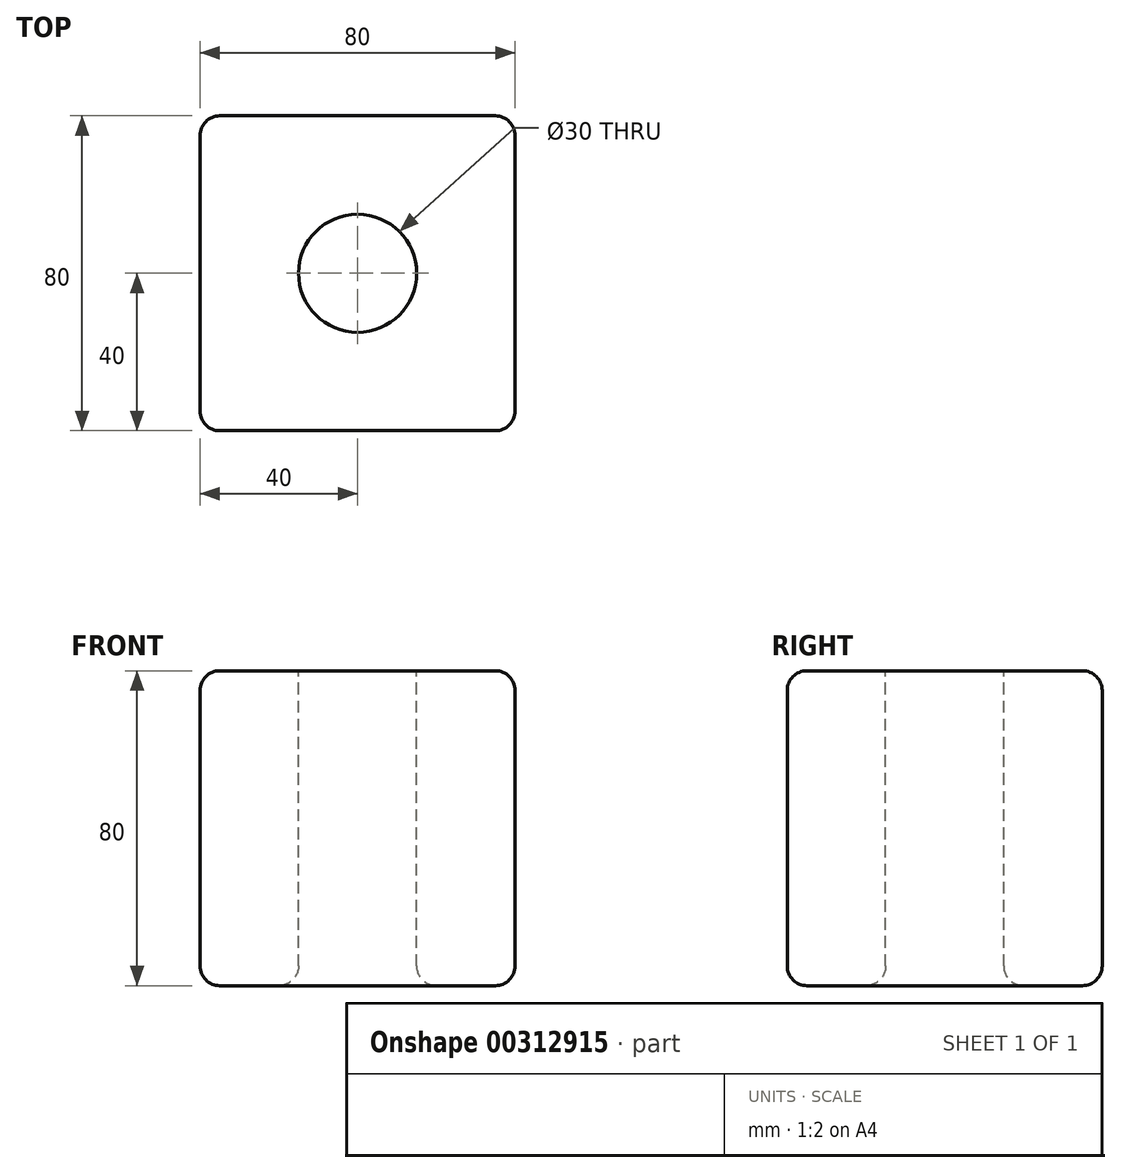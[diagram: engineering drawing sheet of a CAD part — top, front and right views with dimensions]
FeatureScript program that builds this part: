
annotation { "Feature Type Name" : "Feature", "Feature Type Description" : "" }
export const myFeature = defineFeature(function(context is Context, id is Id, definition is map)
    precondition{}
    {
        {
            var Q0;
            Q0=qCreatedBy(makeId("Top.planeOp"),FACE);
            var sketch = newSketch(context, id + "F0", { "sketchPlane" : qUnion([Q0])});
            skLineSegment(sketch, "E0.bottom", {"start": v(40, -40) * mm, "end": v(-40, -40) * mm});
            skLineSegment(sketch, "E0.top", {"start": v(40, 40) * mm, "end": v(-40, 40) * mm});
            skLineSegment(sketch, "E0.left", {"start": v(40, -40) * mm, "end": v(40, 40) * mm});
            skLineSegment(sketch, "E0.right", {"start": v(-40, -40) * mm, "end": v(-40, 40) * mm});
            skPoint(sketch, "E0.middle", {"position": v(0, 0) * mm});
            skSolve(sketch);
        }
        {
            var Q0;
            Q0=makeQuery(id+"F0.imprint","IMPRINT",FACE,{"disambiguationData":[TD([[makeQuery(id+"F0.imprint","IMPRINT",EDGE,{"derivedFrom":sQuery(id+"F0.wireOp",EDGE,"E0.bottom")}),-1.0]])]});
            extrude(context, id + "F1", {"entities" : qUnion([Q0]), "endBound" : BoundingType.SYMMETRIC, "depth" : 80 * mm});
        }
        {
            var Q0;
            Q0=makeQuery(id+"F1.opExtrude","CAP_EDGE",EDGE,{"disambiguationData":[OSD([sQuery(id+"F0.wireOp",EDGE,"E0.bottom")])],"isStart":false});
            var Q1;
            Q1=makeQuery(id+"F1.opExtrude","CAP_EDGE",EDGE,{"disambiguationData":[OSD([sQuery(id+"F0.wireOp",EDGE,"E0.bottom")])],"isStart":true});
            var Q2;
            Q2=makeQuery(id+"F1.opExtrude","CAP_EDGE",EDGE,{"disambiguationData":[OSD([sQuery(id+"F0.wireOp",EDGE,"E0.top")])],"isStart":false});
            var Q3;
            Q3=makeQuery(id+"F1.opExtrude","CAP_EDGE",EDGE,{"disambiguationData":[OSD([sQuery(id+"F0.wireOp",EDGE,"E0.top")])],"isStart":true});
            var Q4;
            Q4=makeQuery(id+"F1.opExtrude","CAP_EDGE",EDGE,{"disambiguationData":[OSD([sQuery(id+"F0.wireOp",EDGE,"E0.right")])],"isStart":false});
            var Q5;
            Q5=makeQuery(id+"F1.opExtrude","CAP_EDGE",EDGE,{"disambiguationData":[OSD([sQuery(id+"F0.wireOp",EDGE,"E0.right")])],"isStart":true});
            var Q6;
            Q6=makeQuery(id+"F1.opExtrude","SWEPT_EDGE",EDGE,{"disambiguationData":[OSD([sQuery(id+"F0.wireOp",EDGE,"E0.top"),sQuery(id+"F0.wireOp",EDGE,"E0.left")])]});
            var Q7;
            Q7=makeQuery(id+"F1.opExtrude","SWEPT_EDGE",EDGE,{"disambiguationData":[OSD([sQuery(id+"F0.wireOp",EDGE,"E0.bottom"),sQuery(id+"F0.wireOp",EDGE,"E0.left")])]});
            var Q8;
            Q8=makeQuery(id+"F1.opExtrude","CAP_EDGE",EDGE,{"disambiguationData":[OSD([sQuery(id+"F0.wireOp",EDGE,"E0.left")])],"isStart":true});
            var Q9;
            Q9=makeQuery(id+"F1.opExtrude","SWEPT_EDGE",EDGE,{"disambiguationData":[OSD([sQuery(id+"F0.wireOp",EDGE,"E0.top"),sQuery(id+"F0.wireOp",EDGE,"E0.right")])]});
            var Q10;
            Q10=makeQuery(id+"F1.opExtrude","SWEPT_EDGE",EDGE,{"disambiguationData":[OSD([sQuery(id+"F0.wireOp",EDGE,"E0.bottom"),sQuery(id+"F0.wireOp",EDGE,"E0.right")])]});
            fillet(context, id + "F2", {"entities" : qUnion([Q0, Q1, Q2, Q3, Q4, Q5, Q6, Q7, Q8, Q9, Q10]), "radius" : 5 * mm, "tangentPropagation" : true, "allowEdgeOverflow" : false});
        }
        {
            var Q0;
            Q0=makeQuery(id+"F1.opExtrude","CAP_EDGE",EDGE,{"disambiguationData":[OSD([sQuery(id+"F0.wireOp",EDGE,"E0.left")])],"isStart":false});
            fillet(context, id + "F3", {"entities" : qUnion([Q0]), "radius" : 5 * mm, "tangentPropagation" : true, "allowEdgeOverflow" : false});
        }
        {
            var Q0;
            Q0=makeQuery(id+"F1.opExtrude","CAP_FACE",FACE,{"disambiguationData":[OSD([sQuery(id+"F0.wireOp",EDGE,"E0.bottom"),sQuery(id+"F0.wireOp",EDGE,"E0.top"),sQuery(id+"F0.wireOp",EDGE,"E0.left"),sQuery(id+"F0.wireOp",EDGE,"E0.right")])],"isStart":false});
            var sketch = newSketch(context, id + "F4", { "sketchPlane" : qUnion([Q0])});
            skCircle(sketch, "E1", {"center": v(0, 0) * mm, "radius": 15 * mm});
            skSolve(sketch);
        }
        {
            var Q0;
            Q0 = qSketchRegion(id + "F4", true);
            extrude(context, id + "F5", {"entities" : qUnion([Q0]), "operationType" : NewBodyOperationType.REMOVE, "endBound" : BoundingType.THROUGH_ALL, "oppositeDirection" : true, "depth" : 25 * mm});
        }
        {
            var Q0;
            Q0=makeQuery(id+"F5.boolean.opBoolean","COPY",EDGE,{"derivedFrom":makeQuery(id+"F5.opExtrude","CAP_EDGE",EDGE,{"disambiguationData":[OSD([sQuery(id+"F4.wireOp",EDGE,"E1")])],"isStart":true})});
            var Q1;
            Q1=makeQuery(id+"F5.boolean.opBoolean","INTERSECT",EDGE,{"derivedFrom":[makeQuery(id+"F1.opExtrude","CAP_FACE",FACE,{"disambiguationData":[OSD([sQuery(id+"F0.wireOp",EDGE,"E0.bottom"),sQuery(id+"F0.wireOp",EDGE,"E0.top"),sQuery(id+"F0.wireOp",EDGE,"E0.left"),sQuery(id+"F0.wireOp",EDGE,"E0.right")])],"isStart":true}),makeQuery(id+"F5.opExtrude","SWEPT_FACE",FACE,{"disambiguationData":[OSD([sQuery(id+"F4.wireOp",EDGE,"E1")])]})]});
            fillet(context, id + "F6", {"entities" : qUnion([Q0, Q1]), "radius" : 5 * mm, "tangentPropagation" : true, "allowEdgeOverflow" : false});
        }
    });
